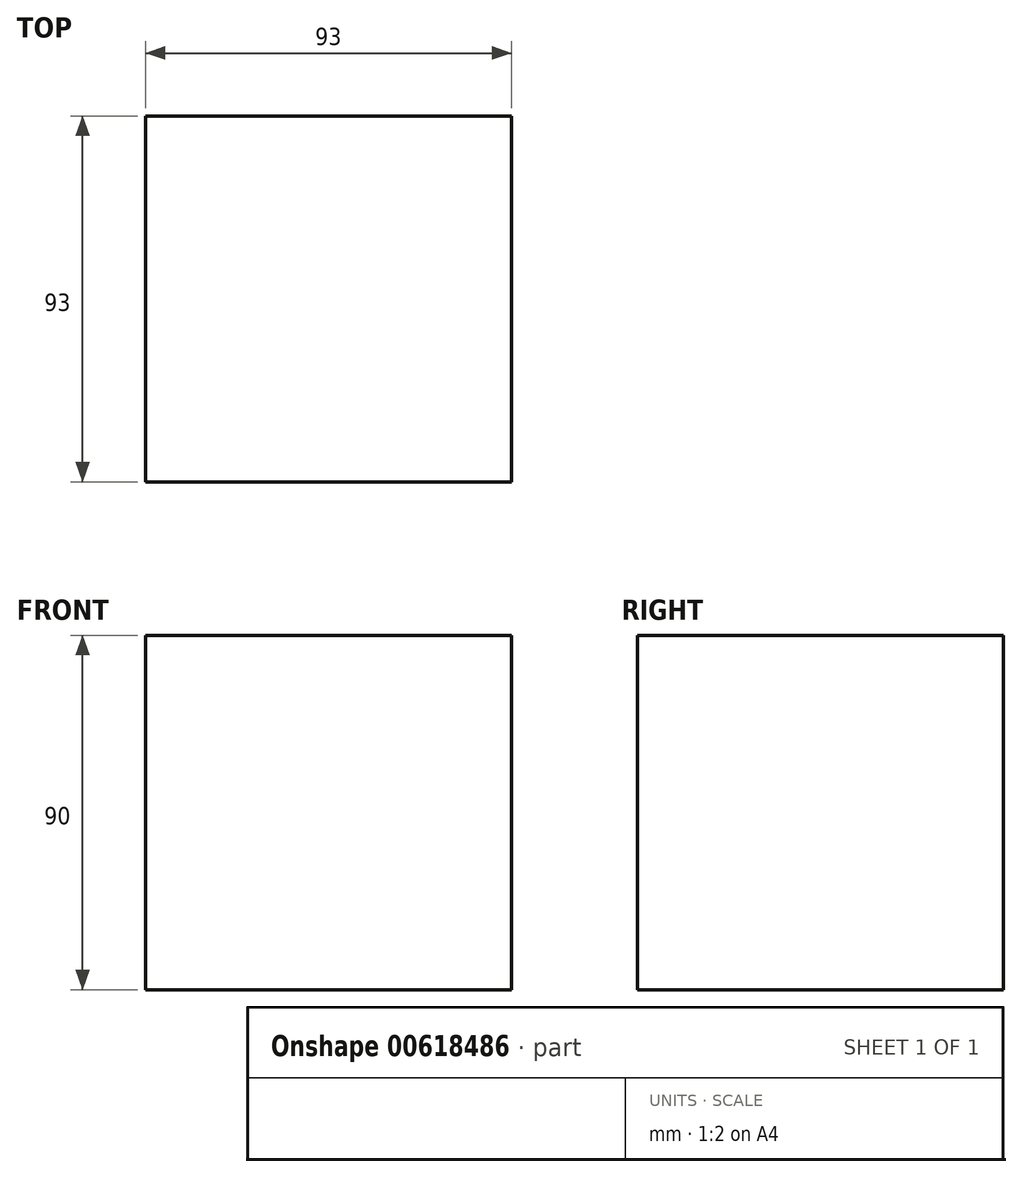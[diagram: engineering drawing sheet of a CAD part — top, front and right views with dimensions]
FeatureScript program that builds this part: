
annotation { "Feature Type Name" : "Feature", "Feature Type Description" : "" }
export const myFeature = defineFeature(function(context is Context, id is Id, definition is map)
    precondition{}
    {
        {
            var Q0;
            Q0=qCreatedBy(makeId("Top.planeOp"),FACE);
            var sketch = newSketch(context, id + "F0", { "sketchPlane" : qUnion([Q0])});
            skLineSegment(sketch, "E0.bottom", {"start": v(0, 0) * mm, "end": v(93, 0) * mm});
            skLineSegment(sketch, "E0.top", {"start": v(0, 93) * mm, "end": v(93, 93) * mm});
            skLineSegment(sketch, "E0.left", {"start": v(0, 0) * mm, "end": v(0, 93) * mm});
            skLineSegment(sketch, "E0.right", {"start": v(93, 0) * mm, "end": v(93, 93) * mm});
            skSolve(sketch);
        }
        {
            var Q0;
            Q0 = qSketchRegion(id + "F0", true);
            extrude(context, id + "F1", {"entities" : qUnion([Q0]), "depth" : 90 * mm, "offsetDistance" : 25.4 * mm});
        }
        {
            var Q0;
            Q0=makeQuery(id+"F1.opExtrude","CAP_FACE",FACE,{"disambiguationData":[OSD([sQuery(id+"F0.wireOp",EDGE,"E0.bottom"),sQuery(id+"F0.wireOp",EDGE,"E0.top"),sQuery(id+"F0.wireOp",EDGE,"E0.left"),sQuery(id+"F0.wireOp",EDGE,"E0.right")])],"isStart":false});
            var sketch = newSketch(context, id + "F2", { "sketchPlane" : qUnion([Q0])});
            skLineSegment(sketch, "E1.bottom", {"start": v(7.62, 50.84) * mm, "end": v(84.62, 50.84) * mm});
            skLineSegment(sketch, "E1.top", {"start": v(7.62, 42.84) * mm, "end": v(84.62, 42.84) * mm});
            skLineSegment(sketch, "E1.left", {"start": v(7.62, 50.84) * mm, "end": v(7.62, 42.84) * mm});
            skLineSegment(sketch, "E1.right", {"start": v(84.62, 50.84) * mm, "end": v(84.62, 42.84) * mm});
            skSolve(sketch);
        }
        {
            var Q0;
            Q0=sQuery(id+"F2.wireOp",EDGE,"E1.left");
            var Q1;
            Q1=sQuery(id+"F2.wireOp",EDGE,"E1.bottom");
            var Q2;
            Q2=sQuery(id+"F2.wireOp",EDGE,"E1.right");
            var Q3;
            Q3=sQuery(id+"F2.wireOp",EDGE,"E1.top");
            extrude(context, id + "F3", {"bodyType" : ToolBodyType.SURFACE, "surfaceEntities" : qUnion([Q0, Q1, Q2, Q3]), "oppositeDirection" : true, "depth" : 5.08 * mm, "offsetDistance" : 25.4 * mm});
        }
    });
